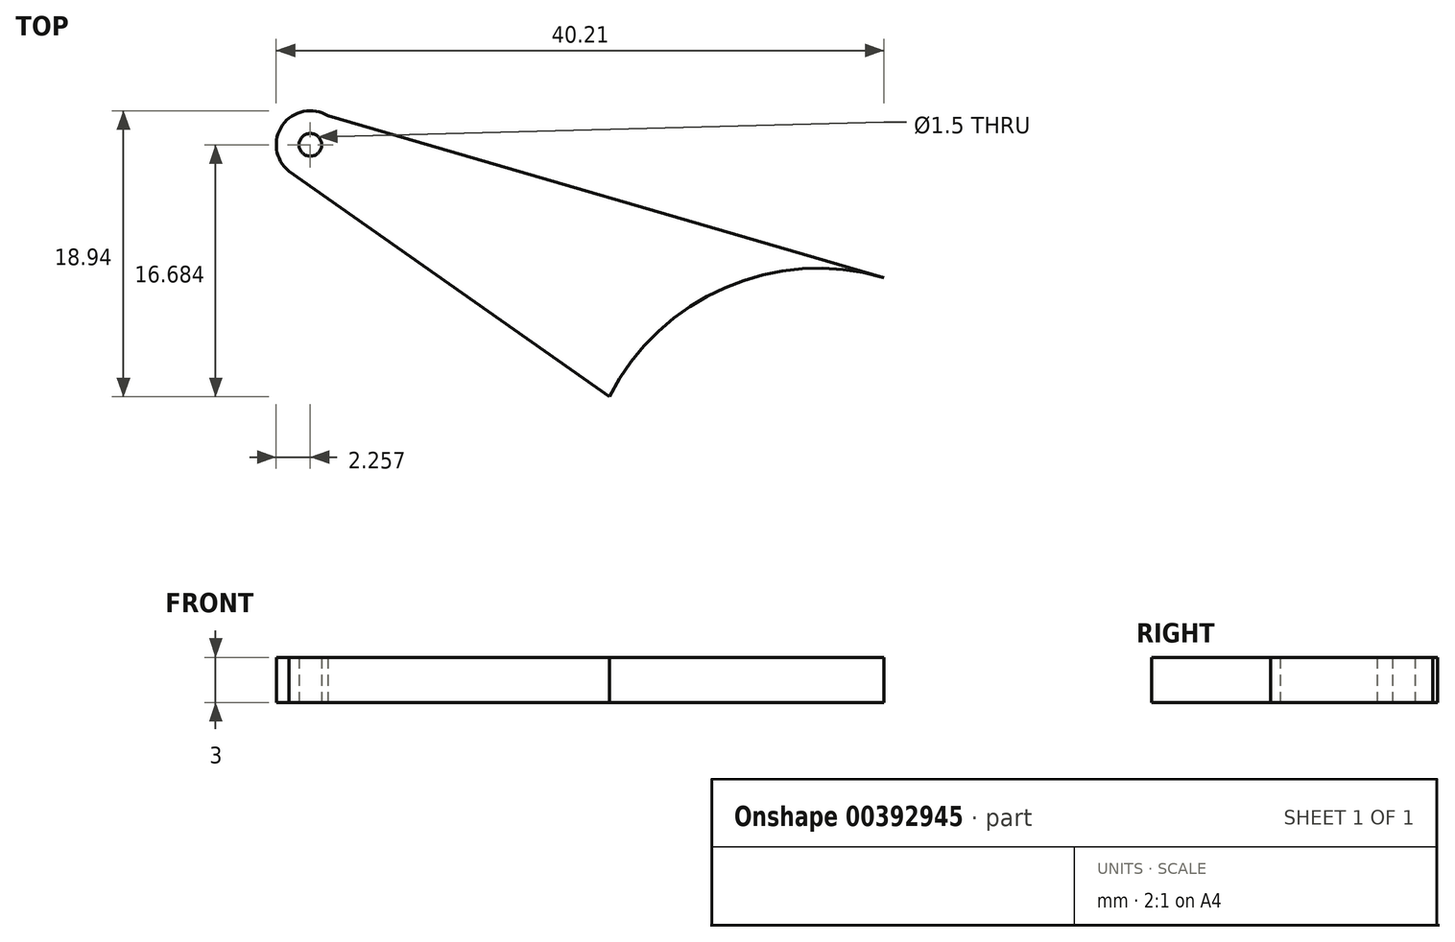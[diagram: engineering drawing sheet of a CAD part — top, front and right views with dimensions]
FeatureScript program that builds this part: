
annotation { "Feature Type Name" : "Feature", "Feature Type Description" : "" }
export const myFeature = defineFeature(function(context is Context, id is Id, definition is map)
    precondition{}
    {
        {
            var Q0;
            Q0=qCreatedBy(makeId("Top.planeOp"),FACE);
            var sketch = newSketch(context, id + "F0", { "sketchPlane" : qUnion([Q0])});
            skCircle(sketch, "E0", {"center": v(0, 0) * mm, "radius": 15.5 * mm});
            skCircle(sketch, "E1", {"center": v(0, 0) * mm, "radius": 0.75 * mm});
            skLineSegment(sketch, "E2", {"start": v(0, 0) * mm, "end": v(-33.61, 23.67) * mm, "construction": true});
            skLineSegment(sketch, "E3", {"start": v(-13.83, 7) * mm, "end": v(-35.03, 21.92) * mm});
            skLineSegment(sketch, "E4", {"start": v(-32.44, 25.6) * mm, "end": v(4.34, 14.88) * mm});
            skArc(sketch, "E5", {"start": v(-32.44, 25.6) * mm, "mid": v(-35.54, 24.85) * mm, "end": v(-34.79, 21.75) * mm});
            skCircle(sketch, "E6", {"center": v(-33.61, 23.67) * mm, "radius": 0.75 * mm});
            skSolve(sketch);
        }
        {
            var Q0;
            {var subQ33=sQuery(id+"F0.wireOp",EDGE,"LihCcqCG-InDh-bhpe-lUBO-M4oIEpqKWyxd");Q0=makeQuery(id+"F0.imprint","IMPRINT",FACE,{"disambiguationData":[TD([[makeQuery(id+"F0.imprint","IMPRINT",EDGE,{"derivedFrom":subQ33}),-1.0]])]});}
            var Q1;
            {var subQ0=sQuery(id+"F0.wireOp",EDGE,"E4");Q1=makeQuery(id+"F0.imprint","IMPRINT",FACE,{"disambiguationData":[TD([[makeQuery(id+"F0.imprint","IMPRINT",EDGE,{"derivedFrom":subQ0}),-1.0]])]});}
            var Q2;
            {var subQ22=sQuery(id+"F0.wireOp",EDGE,"86585395-389c-45ea-92c6-77ffceb5c8d9.11.0");Q2=makeQuery(id+"F0.imprint","IMPRINT",FACE,{"disambiguationData":[TD([[makeQuery(id+"F0.imprint","IMPRINT",EDGE,{"derivedFrom":subQ22}),1.0]])]});}
            extrude(context, id + "F1", {"entities" : qUnion([Q0, Q1, Q2]), "depth" : 3 * mm});
        }
    });
